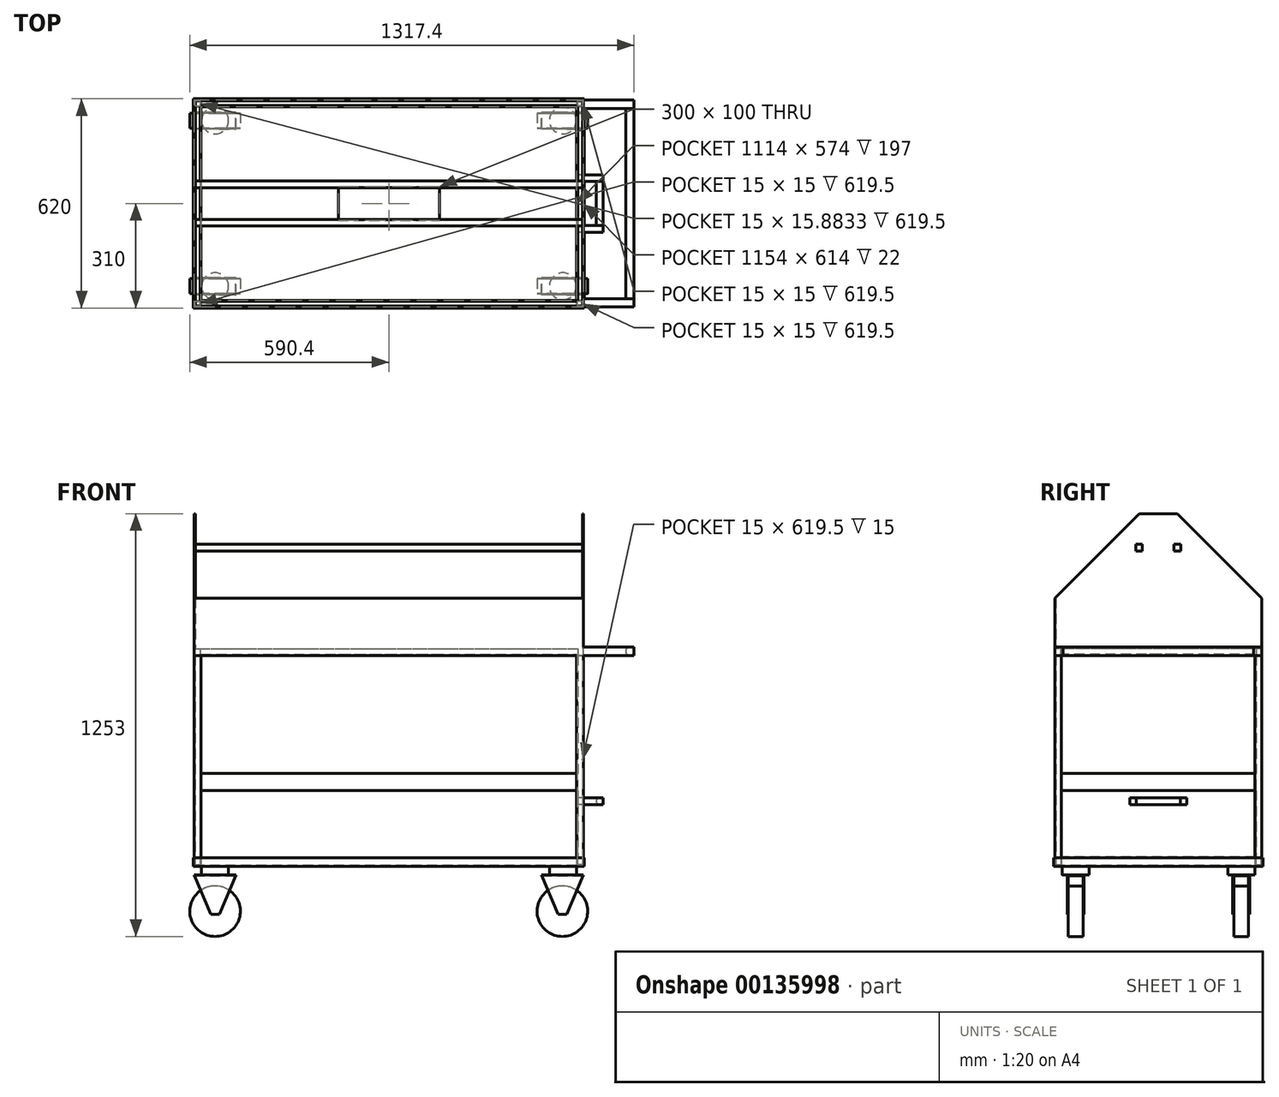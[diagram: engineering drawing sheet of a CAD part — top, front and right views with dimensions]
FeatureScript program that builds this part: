
annotation { "Feature Type Name" : "Feature", "Feature Type Description" : "" }
export const myFeature = defineFeature(function(context is Context, id is Id, definition is map)
    precondition{}
    {
        {
            var Q0;
            Q0=qCreatedBy(makeId("Top.planeOp"),FACE);
            var sketch = newSketch(context, id + "F0", { "sketchPlane" : qUnion([Q0])});
            skLineSegment(sketch, "E0.bottom", {"start": v(-580, 310) * mm, "end": v(580, 310) * mm});
            skLineSegment(sketch, "E0.top", {"start": v(-580, -310) * mm, "end": v(580, -310) * mm});
            skLineSegment(sketch, "E0.left", {"start": v(-580, 310) * mm, "end": v(-580, -310) * mm});
            skLineSegment(sketch, "E0.right", {"start": v(580, 310) * mm, "end": v(580, -310) * mm});
            skPoint(sketch, "E0.middle", {"position": v(0, 0) * mm});
            skLineSegment(sketch, "E1.bottom", {"start": v(-560, 290) * mm, "end": v(560, 290) * mm});
            skLineSegment(sketch, "E1.top", {"start": v(-560, -290) * mm, "end": v(560, -290) * mm});
            skLineSegment(sketch, "E1.left", {"start": v(-560, 290) * mm, "end": v(-560, -290) * mm});
            skLineSegment(sketch, "E1.right", {"start": v(560, 290) * mm, "end": v(560, -290) * mm});
            skSolve(sketch);
        }
        {
            var Q0;
            Q0=makeQuery(id+"F0.imprint","IMPRINT",FACE,{"disambiguationData":[TD([[makeQuery(id+"F0.imprint","IMPRINT",EDGE,{"derivedFrom":sQuery(id+"F0.wireOp",EDGE,"E1.bottom")}),-1.0]])]});
            extrude(context, id + "F1", {"entities" : qUnion([Q0]), "depth" : 350 * mm});
        }
        {
            var Q0;
            Q0=makeQuery(id+"F0.imprint","IMPRINT",FACE,{"disambiguationData":[TD([[makeQuery(id+"F0.imprint","IMPRINT",EDGE,{"derivedFrom":sQuery(id+"F0.wireOp",EDGE,"E1.bottom")}),-1.0]])]});
            extrude(context, id + "F2", {"entities" : qUnion([Q0]), "operationType" : NewBodyOperationType.ADD, "oppositeDirection" : true, "depth" : 250 * mm});
        }
        {
            var Q0;
            Q0=makeQuery(id+"F0.imprint","IMPRINT",FACE,{"disambiguationData":[TD([[makeQuery(id+"F0.imprint","IMPRINT",EDGE,{"derivedFrom":sQuery(id+"F0.wireOp",EDGE,"E1.bottom")}),-1.0]])]});
            extrude(context, id + "F3", {"entities" : qUnion([Q0]), "operationType" : NewBodyOperationType.REMOVE, "oppositeDirection" : true, "depth" : 50 * mm});
        }
        {
            var Q0;
            Q0=makeQuery(id+"F3.boolean.opBoolean","COPY",FACE,{"derivedFrom":makeQuery(id+"F3.opExtrude","CAP_FACE",FACE,{"disambiguationData":[OSD([sQuery(id+"F0.wireOp",EDGE,"E1.bottom"),sQuery(id+"F0.wireOp",EDGE,"E1.top"),sQuery(id+"F0.wireOp",EDGE,"E1.left"),sQuery(id+"F0.wireOp",EDGE,"E1.right")])],"isStart":false})});
            shell(context, id + "F4", {"entities" : qUnion([Q0]), "thickness" : 3 * mm});
        }
        {
            var Q0;
            Q0=makeQuery(id+"F2.opExtrude","CAP_FACE",FACE,{"disambiguationData":[OSD([sQuery(id+"F0.wireOp",EDGE,"E1.bottom"),sQuery(id+"F0.wireOp",EDGE,"E1.top"),sQuery(id+"F0.wireOp",EDGE,"E1.left"),sQuery(id+"F0.wireOp",EDGE,"E1.right")])],"isStart":false});
            var sketch = newSketch(context, id + "F5", { "sketchPlane" : qUnion([Q0])});
            skLineSegment(sketch, "E2.bottom", {"start": v(-580, 310) * mm, "end": v(580, 310) * mm});
            skLineSegment(sketch, "E2.top", {"start": v(-580, -310) * mm, "end": v(580, -310) * mm});
            skLineSegment(sketch, "E2.left", {"start": v(-580, 310) * mm, "end": v(-580, -310) * mm});
            skLineSegment(sketch, "E2.right", {"start": v(580, 310) * mm, "end": v(580, -310) * mm});
            skPoint(sketch, "E2.middle", {"position": v(0, 0) * mm});
            skSolve(sketch);
        }
        {
            var Q0;
            Q0=makeQuery(id+"F5.imprint","IMPRINT",FACE,{"disambiguationData":[TD([[makeQuery(id+"F5.imprint","IMPRINT",EDGE,{"derivedFrom":sQuery(id+"F5.wireOp",EDGE,"E2.bottom")}),-1.0]])]});
            var Q1;
            Q1=makeQuery(id+"F5.imprint","IMPRINT",FACE,{"disambiguationData":[TD([[makeQuery(id+"F5.imprint","IMPRINT",EDGE,{"derivedFrom":makeQuery(id+"F2.opExtrude","CAP_EDGE",EDGE,{"disambiguationData":[OSD([sQuery(id+"F0.wireOp",EDGE,"E1.bottom")])],"isStart":false})}),1.0]])]});
            extrude(context, id + "F6", {"entities" : qUnion([Q0, Q1]), "depth" : 25 * mm});
        }
        {
            var Q0;
            Q0=makeQuery(id+"F6.opExtrude","CAP_FACE",FACE,{"disambiguationData":[OSD([sQuery(id+"F5.wireOp",EDGE,"E2.bottom"),sQuery(id+"F5.wireOp",EDGE,"E2.top"),sQuery(id+"F5.wireOp",EDGE,"E2.left"),sQuery(id+"F5.wireOp",EDGE,"E2.right")])],"isStart":true});
            var Q1;
            Q1=makeQuery(id+"F6.opExtrude","SWEPT_BODY",BODY,{"disambiguationData":[OSD([sQuery(id+"F5.wireOp",EDGE,"E2.bottom"),sQuery(id+"F5.wireOp",EDGE,"E2.top"),sQuery(id+"F5.wireOp",EDGE,"E2.left"),sQuery(id+"F5.wireOp",EDGE,"E2.right")])]});
            shell(context, id + "F7", {"entities" : qUnion([Q0]), "parts" : qUnion([Q1]), "thickness" : 3 * mm});
        }
        {
            var Q0;
            Q0=makeQuery(id+"F7.opShell","OFFSET_FACE",FACE,{"disambiguationData":[OSD([sQuery(id+"F5.wireOp",EDGE,"E2.bottom"),sQuery(id+"F5.wireOp",EDGE,"E2.top"),sQuery(id+"F5.wireOp",EDGE,"E2.left"),sQuery(id+"F5.wireOp",EDGE,"E2.right")])]});
            var sketch = newSketch(context, id + "F8", { "sketchPlane" : qUnion([Q0])});
            skLineSegment(sketch, "E3.bottom", {"start": v(-577, 307) * mm, "end": v(-557, 307) * mm});
            skLineSegment(sketch, "E3.top", {"start": v(-577, 286.12) * mm, "end": v(-557, 286.12) * mm});
            skLineSegment(sketch, "E3.left", {"start": v(-577, 307) * mm, "end": v(-577, 286.12) * mm});
            skLineSegment(sketch, "E3.right", {"start": v(-557, 307) * mm, "end": v(-557, 286.12) * mm});
            skLineSegment(sketch, "E4.bottom", {"start": v(577, 307) * mm, "end": v(557, 307) * mm});
            skLineSegment(sketch, "E4.top", {"start": v(577, 287) * mm, "end": v(557, 287) * mm});
            skLineSegment(sketch, "E4.left", {"start": v(577, 307) * mm, "end": v(577, 287) * mm});
            skLineSegment(sketch, "E4.right", {"start": v(557, 307) * mm, "end": v(557, 287) * mm});
            skLineSegment(sketch, "E5.bottom", {"start": v(577, -307) * mm, "end": v(557, -307) * mm});
            skLineSegment(sketch, "E5.top", {"start": v(577, -287) * mm, "end": v(557, -287) * mm});
            skLineSegment(sketch, "E5.left", {"start": v(577, -307) * mm, "end": v(577, -287) * mm});
            skLineSegment(sketch, "E5.right", {"start": v(557, -307) * mm, "end": v(557, -287) * mm});
            skLineSegment(sketch, "E6.bottom", {"start": v(-577, -307) * mm, "end": v(-557, -307) * mm});
            skLineSegment(sketch, "E6.top", {"start": v(-577, -287) * mm, "end": v(-557, -287) * mm});
            skLineSegment(sketch, "E6.left", {"start": v(-577, -307) * mm, "end": v(-577, -287) * mm});
            skLineSegment(sketch, "E6.right", {"start": v(-557, -307) * mm, "end": v(-557, -287) * mm});
            skSolve(sketch);
        }
        {
            var Q0;
            Q0=makeQuery(id+"F8.imprint","IMPRINT",FACE,{"disambiguationData":[TD([[makeQuery(id+"F8.imprint","IMPRINT",EDGE,{"derivedFrom":sQuery(id+"F8.wireOp",EDGE,"E3.bottom")}),-1.0]])]});
            var Q1;
            Q1=makeQuery(id+"F8.imprint","IMPRINT",FACE,{"disambiguationData":[TD([[makeQuery(id+"F8.imprint","IMPRINT",EDGE,{"derivedFrom":sQuery(id+"F8.wireOp",EDGE,"E6.bottom")}),1.0]])]});
            var Q2;
            Q2=makeQuery(id+"F8.imprint","IMPRINT",FACE,{"disambiguationData":[TD([[makeQuery(id+"F8.imprint","IMPRINT",EDGE,{"derivedFrom":sQuery(id+"F8.wireOp",EDGE,"E4.bottom")}),-1.0]])]});
            var Q3;
            Q3=makeQuery(id+"F8.imprint","IMPRINT",FACE,{"disambiguationData":[TD([[makeQuery(id+"F8.imprint","IMPRINT",EDGE,{"derivedFrom":sQuery(id+"F8.wireOp",EDGE,"E5.bottom")}),1.0]])]});
            extrude(context, id + "F9", {"entities" : qUnion([Q0, Q1, Q2, Q3]), "depth" : 622 * mm});
        }
        {
            var Q0;
            Q0=makeQuery(id+"F9.opExtrude","CAP_FACE",FACE,{"disambiguationData":[OSD([sQuery(id+"F8.wireOp",EDGE,"E3.bottom"),sQuery(id+"F8.wireOp",EDGE,"E3.top"),sQuery(id+"F8.wireOp",EDGE,"E3.left"),sQuery(id+"F8.wireOp",EDGE,"E3.right")])],"isStart":false});
            var Q1;
            Q1=makeQuery(id+"F9.opExtrude","CAP_FACE",FACE,{"disambiguationData":[OSD([sQuery(id+"F8.wireOp",EDGE,"E4.bottom"),sQuery(id+"F8.wireOp",EDGE,"E4.top"),sQuery(id+"F8.wireOp",EDGE,"E4.left"),sQuery(id+"F8.wireOp",EDGE,"E4.right")])],"isStart":false});
            var Q2;
            Q2=makeQuery(id+"F9.opExtrude","CAP_FACE",FACE,{"disambiguationData":[OSD([sQuery(id+"F8.wireOp",EDGE,"E5.bottom"),sQuery(id+"F8.wireOp",EDGE,"E5.top"),sQuery(id+"F8.wireOp",EDGE,"E5.left"),sQuery(id+"F8.wireOp",EDGE,"E5.right")])],"isStart":false});
            var Q3;
            Q3=makeQuery(id+"F9.opExtrude","CAP_FACE",FACE,{"disambiguationData":[OSD([sQuery(id+"F8.wireOp",EDGE,"E6.bottom"),sQuery(id+"F8.wireOp",EDGE,"E6.top"),sQuery(id+"F8.wireOp",EDGE,"E6.left"),sQuery(id+"F8.wireOp",EDGE,"E6.right")])],"isStart":false});
            shell(context, id + "F10", {"entities" : qUnion([Q0, Q1, Q2, Q3]), "thickness" : 2.5 * mm});
        }
        {
            var Q0;
            Q0=makeQuery(id+"F1.opExtrude","CAP_FACE",FACE,{"disambiguationData":[OSD([sQuery(id+"F0.wireOp",EDGE,"E1.bottom"),sQuery(id+"F0.wireOp",EDGE,"E1.top"),sQuery(id+"F0.wireOp",EDGE,"E1.left"),sQuery(id+"F0.wireOp",EDGE,"E1.right")])],"isStart":false});
            var sketch = newSketch(context, id + "F11", { "sketchPlane" : qUnion([Q0])});
            skLineSegment(sketch, "E7.bottom", {"start": v(-577, 307) * mm, "end": v(577, 307) * mm});
            skLineSegment(sketch, "E7.top", {"start": v(-577, -307) * mm, "end": v(577, -307) * mm});
            skLineSegment(sketch, "E7.left", {"start": v(-577, 307) * mm, "end": v(-577, -307) * mm});
            skLineSegment(sketch, "E7.right", {"start": v(577, 307) * mm, "end": v(577, -307) * mm});
            skPoint(sketch, "E7.middle", {"position": v(0, 0) * mm});
            skSolve(sketch);
        }
        {
            var Q0;
            Q0=makeQuery(id+"F11.imprint","IMPRINT",FACE,{"disambiguationData":[TD([[makeQuery(id+"F11.imprint","IMPRINT",EDGE,{"derivedFrom":sQuery(id+"F11.wireOp",EDGE,"E7.bottom")}),-1.0]])]});
            extrude(context, id + "F12", {"entities" : qUnion([Q0]), "depth" : 20 * mm});
        }
        {
            var Q0;
            Q0=makeQuery(id+"F12.opExtrude","CAP_FACE",FACE,{"disambiguationData":[OSD([sQuery(id+"F0.wireOp",EDGE,"E1.bottom"),sQuery(id+"F0.wireOp",EDGE,"E1.top"),sQuery(id+"F0.wireOp",EDGE,"E1.left"),sQuery(id+"F0.wireOp",EDGE,"E1.right"),sQuery(id+"F33Y3pSXNLTwZaf_1.wireOp",EDGE,"aj6i3p2y-FQMm-kt0m-HM5S-YSBZW6WqoPSV"),sQuery(id+"F33Y3pSXNLTwZaf_1.wireOp",EDGE,"CZkD7vCU-3LIm-oKTz-ViHN-LZSoxyDXXNPL"),sQuery(id+"F33Y3pSXNLTwZaf_1.wireOp",EDGE,"GoPMTof5-LQTN-zhxn-LOWR-9AagRQIQ8QUd"),sQuery(id+"F33Y3pSXNLTwZaf_1.wireOp",EDGE,"wMd1c553-RlNz-IpVQ-kuJJ-040cahTZoC20"),sQuery(id+"F1xDDwHVUP71mYk_1.wireOp",EDGE,"cAczI6bI-1LX6-aqdC-7smG-W6fWwqjZtxQi"),sQuery(id+"F1xDDwHVUP71mYk_1.wireOp",EDGE,"ZDiwBjCm-7RDb-v4AQ-MkSP-Jul3cs5UostI"),sQuery(id+"F1xDDwHVUP71mYk_1.wireOp",EDGE,"UBjxF51A-ai0a-dGns-wWAK-TeR3P6ofujuV"),sQuery(id+"F1xDDwHVUP71mYk_1.wireOp",EDGE,"N02EDcg1-XUBP-QACv-A8dY-pTifU5Cc8YaH"),sQuery(id+"F11.wireOp",EDGE,"E7.bottom"),sQuery(id+"F11.wireOp",EDGE,"E7.top"),sQuery(id+"F11.wireOp",EDGE,"E7.left"),sQuery(id+"F11.wireOp",EDGE,"E7.right")])],"isStart":false});
            var sketch = newSketch(context, id + "F13", { "sketchPlane" : qUnion([Q0])});
            skLineSegment(sketch, "E8.bottom", {"start": v(-577, 307) * mm, "end": v(-574, 307) * mm});
            skLineSegment(sketch, "E8.top", {"start": v(-577, -307) * mm, "end": v(-574, -307) * mm});
            skLineSegment(sketch, "E8.left", {"start": v(-577, 307) * mm, "end": v(-577, -307) * mm});
            skLineSegment(sketch, "E8.right", {"start": v(-574, 307) * mm, "end": v(-574, -307) * mm});
            skLineSegment(sketch, "E9.bottom", {"start": v(577, -307) * mm, "end": v(574, -307) * mm});
            skLineSegment(sketch, "E9.top", {"start": v(577, 307) * mm, "end": v(574, 307) * mm});
            skLineSegment(sketch, "E9.left", {"start": v(577, -307) * mm, "end": v(577, 307) * mm});
            skLineSegment(sketch, "E9.right", {"start": v(574, -307) * mm, "end": v(574, 307) * mm});
            skSolve(sketch);
        }
        {
            var Q0;
            Q0=makeQuery(id+"F13.imprint","IMPRINT",FACE,{"disambiguationData":[TD([[makeQuery(id+"F13.imprint","IMPRINT",EDGE,{"derivedFrom":sQuery(id+"F13.wireOp",EDGE,"E9.bottom")}),1.0]])]});
            var Q1;
            Q1=makeQuery(id+"F13.imprint","IMPRINT",FACE,{"disambiguationData":[TD([[makeQuery(id+"F13.imprint","IMPRINT",EDGE,{"derivedFrom":sQuery(id+"F13.wireOp",EDGE,"E8.bottom")}),-1.0]])]});
            extrude(context, id + "F14", {"entities" : qUnion([Q0, Q1]), "operationType" : NewBodyOperationType.ADD, "depth" : 400 * mm});
        }
        {
            var Q0;
            Q0=makeQuery(id+"F14.boolean.opBoolean","MERGE",FACE,{"derivedFrom":[makeQuery(id+"F12.opExtrude","SWEPT_FACE",FACE,{"disambiguationData":[OSD([sQuery(id+"F11.wireOp",EDGE,"E7.right")])]}),makeQuery(id+"F14.opExtrude","SWEPT_FACE",FACE,{"disambiguationData":[OSD([sQuery(id+"F13.wireOp",EDGE,"E9.left")])]})]});
            var sketch = newSketch(context, id + "F15", { "sketchPlane" : qUnion([Q0])});
            skLineSegment(sketch, "E10", {"start": v(-307, 770) * mm, "end": v(-57, 770) * mm});
            skLineSegment(sketch, "E11", {"start": v(-307, 770) * mm, "end": v(-307, 520) * mm});
            skLineSegment(sketch, "E12", {"start": v(-307, 520) * mm, "end": v(-57, 770) * mm});
            skLineSegment(sketch, "E13", {"start": v(307, 770) * mm, "end": v(57, 770) * mm});
            skLineSegment(sketch, "E14", {"start": v(57, 770) * mm, "end": v(307, 520) * mm});
            skLineSegment(sketch, "E15", {"start": v(307, 520) * mm, "end": v(307, 770) * mm});
            skLineSegment(sketch, "E16", {"start": v(-307, 770) * mm, "end": v(-307, 670) * mm, "construction": true});
            skLineSegment(sketch, "E17.bottom", {"start": v(-77.82, 670.93) * mm, "end": v(-57.82, 670.93) * mm});
            skLineSegment(sketch, "E17.top", {"start": v(-77.82, 650.93) * mm, "end": v(-57.82, 650.93) * mm});
            skLineSegment(sketch, "E17.left", {"start": v(-77.82, 670.93) * mm, "end": v(-77.82, 650.93) * mm});
            skLineSegment(sketch, "E17.right", {"start": v(-57.82, 670.93) * mm, "end": v(-57.82, 650.93) * mm});
            skPoint(sketch, "E17.middle", {"position": v(-67.82, 660.93) * mm});
            skLineSegment(sketch, "E18.bottom", {"start": v(31.3, 667.95) * mm, "end": v(51.3, 667.95) * mm});
            skLineSegment(sketch, "E18.top", {"start": v(31.3, 647.95) * mm, "end": v(51.3, 647.95) * mm});
            skLineSegment(sketch, "E18.left", {"start": v(31.3, 667.95) * mm, "end": v(31.3, 647.95) * mm});
            skLineSegment(sketch, "E18.right", {"start": v(51.3, 667.95) * mm, "end": v(51.3, 647.95) * mm});
            skPoint(sketch, "E18.middle", {"position": v(41.3, 657.95) * mm});
            skSolve(sketch);
        }
        {
            var Q0;
            Q0=makeQuery(id+"F15.imprint","IMPRINT",FACE,{"disambiguationData":[TD([[makeQuery(id+"F15.imprint","IMPRINT",EDGE,{"derivedFrom":sQuery(id+"F15.wireOp",EDGE,"E10")}),1.0]])]});
            var Q1;
            Q1=makeQuery(id+"F15.imprint","IMPRINT",FACE,{"disambiguationData":[TD([[makeQuery(id+"F15.imprint","IMPRINT",EDGE,{"derivedFrom":sQuery(id+"F15.wireOp",EDGE,"E13")}),1.0]])]});
            extrude(context, id + "F16", {"entities" : qUnion([Q0, Q1]), "operationType" : NewBodyOperationType.REMOVE, "oppositeDirection" : true, "depth" : 1160 * mm});
        }
        {
            var Q0;
            Q0=makeQuery(id+"F14.boolean.opBoolean","MERGE",FACE,{"derivedFrom":[makeQuery(id+"F12.opExtrude","SWEPT_FACE",FACE,{"disambiguationData":[OSD([sQuery(id+"F11.wireOp",EDGE,"E7.right")])]}),makeQuery(id+"F14.opExtrude","SWEPT_FACE",FACE,{"disambiguationData":[OSD([sQuery(id+"F13.wireOp",EDGE,"E9.left")])]})]});
            var sketch = newSketch(context, id + "F17", { "sketchPlane" : qUnion([Q0])});
            skLineSegment(sketch, "E19", {"start": v(-57, 770) * mm, "end": v(-57, 670) * mm, "construction": true});
            skLineSegment(sketch, "E20", {"start": v(57, 770) * mm, "end": v(57, 670) * mm, "construction": true});
            skLineSegment(sketch, "E21.bottom", {"start": v(-67, 680) * mm, "end": v(-47, 680) * mm});
            skLineSegment(sketch, "E21.top", {"start": v(-67, 660) * mm, "end": v(-47, 660) * mm});
            skLineSegment(sketch, "E21.left", {"start": v(-67, 680) * mm, "end": v(-67, 660) * mm});
            skLineSegment(sketch, "E21.right", {"start": v(-47, 680) * mm, "end": v(-47, 660) * mm});
            skPoint(sketch, "E21.middle", {"position": v(-57, 670) * mm});
            skLineSegment(sketch, "E22.bottom", {"start": v(47, 680) * mm, "end": v(67, 680) * mm});
            skLineSegment(sketch, "E22.top", {"start": v(47, 660) * mm, "end": v(67, 660) * mm});
            skLineSegment(sketch, "E22.left", {"start": v(47, 680) * mm, "end": v(47, 660) * mm});
            skLineSegment(sketch, "E22.right", {"start": v(67, 680) * mm, "end": v(67, 660) * mm});
            skPoint(sketch, "E22.middle", {"position": v(57, 670) * mm});
            skSolve(sketch);
        }
        {
            var Q0;
            Q0=makeQuery(id+"F17.imprint","IMPRINT",FACE,{"disambiguationData":[TD([[makeQuery(id+"F17.imprint","IMPRINT",EDGE,{"derivedFrom":sQuery(id+"F17.wireOp",EDGE,"E21.bottom")}),-1.0]])]});
            var Q1;
            Q1=makeQuery(id+"F17.imprint","IMPRINT",FACE,{"disambiguationData":[TD([[makeQuery(id+"F17.imprint","IMPRINT",EDGE,{"derivedFrom":sQuery(id+"F17.wireOp",EDGE,"E22.bottom")}),-1.0]])]});
            extrude(context, id + "F18", {"entities" : qUnion([Q0, Q1]), "oppositeDirection" : true, "offsetDistance" : 25 * mm, "depth" : 1153 * mm});
        }
        {
            var Q0;
            Q0=makeQuery(id+"F12.opExtrude","CAP_FACE",FACE,{"disambiguationData":[OSD([sQuery(id+"F0.wireOp",EDGE,"E1.bottom"),sQuery(id+"F0.wireOp",EDGE,"E1.top"),sQuery(id+"F0.wireOp",EDGE,"E1.left"),sQuery(id+"F0.wireOp",EDGE,"E1.right"),sQuery(id+"F33Y3pSXNLTwZaf_1.wireOp",EDGE,"aj6i3p2y-FQMm-kt0m-HM5S-YSBZW6WqoPSV"),sQuery(id+"F33Y3pSXNLTwZaf_1.wireOp",EDGE,"CZkD7vCU-3LIm-oKTz-ViHN-LZSoxyDXXNPL"),sQuery(id+"F33Y3pSXNLTwZaf_1.wireOp",EDGE,"GoPMTof5-LQTN-zhxn-LOWR-9AagRQIQ8QUd"),sQuery(id+"F33Y3pSXNLTwZaf_1.wireOp",EDGE,"wMd1c553-RlNz-IpVQ-kuJJ-040cahTZoC20"),sQuery(id+"F1xDDwHVUP71mYk_1.wireOp",EDGE,"cAczI6bI-1LX6-aqdC-7smG-W6fWwqjZtxQi"),sQuery(id+"F1xDDwHVUP71mYk_1.wireOp",EDGE,"ZDiwBjCm-7RDb-v4AQ-MkSP-Jul3cs5UostI"),sQuery(id+"F1xDDwHVUP71mYk_1.wireOp",EDGE,"UBjxF51A-ai0a-dGns-wWAK-TeR3P6ofujuV"),sQuery(id+"F1xDDwHVUP71mYk_1.wireOp",EDGE,"N02EDcg1-XUBP-QACv-A8dY-pTifU5Cc8YaH"),sQuery(id+"F11.wireOp",EDGE,"E7.bottom"),sQuery(id+"F11.wireOp",EDGE,"E7.top"),sQuery(id+"F11.wireOp",EDGE,"E7.left"),sQuery(id+"F11.wireOp",EDGE,"E7.right")])],"isStart":false});
            var sketch = newSketch(context, id + "F19", { "sketchPlane" : qUnion([Q0])});
            skLineSegment(sketch, "E23.bottom", {"start": v(-574, 307) * mm, "end": v(574, 307) * mm});
            skLineSegment(sketch, "E23.top", {"start": v(-574, 304) * mm, "end": v(574, 304) * mm});
            skLineSegment(sketch, "E23.left", {"start": v(-574, 307) * mm, "end": v(-574, 304) * mm});
            skLineSegment(sketch, "E23.right", {"start": v(574, 307) * mm, "end": v(574, 304) * mm});
            skLineSegment(sketch, "E24.bottom", {"start": v(-574, -307) * mm, "end": v(574, -307) * mm});
            skLineSegment(sketch, "E24.top", {"start": v(-574, -304) * mm, "end": v(574, -304) * mm});
            skLineSegment(sketch, "E24.left", {"start": v(-574, -307) * mm, "end": v(-574, -304) * mm});
            skLineSegment(sketch, "E24.right", {"start": v(574, -307) * mm, "end": v(574, -304) * mm});
            skSolve(sketch);
        }
        {
            var Q0;
            Q0=makeQuery(id+"F19.imprint","IMPRINT",FACE,{"disambiguationData":[TD([[makeQuery(id+"F19.imprint","IMPRINT",EDGE,{"derivedFrom":sQuery(id+"F19.wireOp",EDGE,"E24.bottom")}),1.0]])]});
            var Q1;
            Q1=makeQuery(id+"F19.imprint","IMPRINT",FACE,{"disambiguationData":[TD([[makeQuery(id+"F19.imprint","IMPRINT",EDGE,{"derivedFrom":sQuery(id+"F19.wireOp",EDGE,"E23.bottom")}),-1.0]])]});
            extrude(context, id + "F20", {"entities" : qUnion([Q0, Q1]), "operationType" : NewBodyOperationType.ADD, "depth" : 20 * mm});
        }
        {
            var Q0;
            Q0=makeQuery(id+"F2.opExtrude","SWEPT_FACE",FACE,{"disambiguationData":[OSD([sQuery(id+"F0.wireOp",EDGE,"E1.right")])]});
            var sketch = newSketch(context, id + "F21", { "sketchPlane" : qUnion([Q0])});
            skLineSegment(sketch, "E25", {"start": v(0, -82.19) * mm, "end": v(-75, -82.19) * mm, "construction": true});
            skLineSegment(sketch, "E26", {"start": v(0, -82.19) * mm, "end": v(75, -82.19) * mm, "construction": true});
            skLineSegment(sketch, "E27.bottom", {"start": v(-85, -72.19) * mm, "end": v(-65, -72.19) * mm});
            skLineSegment(sketch, "E27.top", {"start": v(-85, -92.19) * mm, "end": v(-65, -92.19) * mm});
            skLineSegment(sketch, "E27.left", {"start": v(-85, -72.19) * mm, "end": v(-85, -92.19) * mm});
            skLineSegment(sketch, "E27.right", {"start": v(-65, -72.19) * mm, "end": v(-65, -92.19) * mm});
            skPoint(sketch, "E27.middle", {"position": v(-75, -82.19) * mm});
            skLineSegment(sketch, "E28.bottom", {"start": v(65, -72.19) * mm, "end": v(85, -72.19) * mm});
            skLineSegment(sketch, "E28.top", {"start": v(65, -92.19) * mm, "end": v(85, -92.19) * mm});
            skLineSegment(sketch, "E28.left", {"start": v(65, -72.19) * mm, "end": v(65, -92.19) * mm});
            skLineSegment(sketch, "E28.right", {"start": v(85, -72.19) * mm, "end": v(85, -92.19) * mm});
            skPoint(sketch, "E28.middle", {"position": v(75, -82.19) * mm});
            skSolve(sketch);
        }
        {
            var Q0;
            Q0=makeQuery(id+"F21.imprint","IMPRINT",FACE,{"disambiguationData":[TD([[makeQuery(id+"F21.imprint","IMPRINT",EDGE,{"derivedFrom":sQuery(id+"F21.wireOp",EDGE,"E27.bottom")}),-1.0]])]});
            var Q1;
            Q1=makeQuery(id+"F21.imprint","IMPRINT",FACE,{"disambiguationData":[TD([[makeQuery(id+"F21.imprint","IMPRINT",EDGE,{"derivedFrom":sQuery(id+"F21.wireOp",EDGE,"E28.bottom")}),-1.0]])]});
            extrude(context, id + "F22", {"entities" : qUnion([Q0, Q1]), "operationType" : NewBodyOperationType.ADD, "depth" : 75 * mm});
        }
        {
            var Q0;
            Q0=makeQuery(id+"F22.opExtrude","SWEPT_FACE",FACE,{"disambiguationData":[OSD([sQuery(id+"F21.wireOp",EDGE,"E28.left")])]});
            var sketch = newSketch(context, id + "F23", { "sketchPlane" : qUnion([Q0])});
            skCircle(sketch, "E29", {"center": v(625, -82.19) * mm, "radius": 10 * mm});
            skSolve(sketch);
        }
        {
            var Q0;
            {var subQ0=sQuery(id+"F23.wireOp",EDGE,"E29");var subQ1=sQuery(id+"F21.wireOp",EDGE,"E28.left");var subQ3=makeQuery(id+"F23.imprint","INTERSECT",VERTEX,{"derivedFrom":[makeQuery(id+"F22.opExtrude","CAP_EDGE",EDGE,{"disambiguationData":[OSD([subQ1])],"isStart":false}),subQ0]});Q0=makeQuery(id+"F23.imprint","IMPRINT",FACE,{"disambiguationData":[TD([[makeQuery(id+"F23.imprint","IMPRINT",EDGE,{"disambiguationData":[TD([[subQ3,-1.0]])],"derivedFrom":subQ0}),1.0]])]});}
            extrude(context, id + "F24", {"entities" : qUnion([Q0]), "operationType" : NewBodyOperationType.ADD, "depth" : 140 * mm});
        }
        {
            var Q0;
            Q0=makeQuery(id+"F14.boolean.opBoolean","MERGE",FACE,{"derivedFrom":[makeQuery(id+"F12.opExtrude","SWEPT_FACE",FACE,{"disambiguationData":[OSD([sQuery(id+"F11.wireOp",EDGE,"E7.right")])]}),makeQuery(id+"F14.opExtrude","SWEPT_FACE",FACE,{"disambiguationData":[OSD([sQuery(id+"F13.wireOp",EDGE,"E9.left")])]})]});
            var sketch = newSketch(context, id + "F25", { "sketchPlane" : qUnion([Q0])});
            skLineSegment(sketch, "E30.bottom", {"start": v(-307, 350) * mm, "end": v(-282, 350) * mm});
            skLineSegment(sketch, "E30.top", {"start": v(-307, 375) * mm, "end": v(-282, 375) * mm});
            skLineSegment(sketch, "E30.left", {"start": v(-307, 350) * mm, "end": v(-307, 375) * mm});
            skLineSegment(sketch, "E30.right", {"start": v(-282, 350) * mm, "end": v(-282, 375) * mm});
            skLineSegment(sketch, "E31.bottom", {"start": v(307, 350) * mm, "end": v(282, 350) * mm});
            skLineSegment(sketch, "E31.top", {"start": v(307, 375) * mm, "end": v(282, 375) * mm});
            skLineSegment(sketch, "E31.left", {"start": v(307, 350) * mm, "end": v(307, 375) * mm});
            skLineSegment(sketch, "E31.right", {"start": v(282, 350) * mm, "end": v(282, 375) * mm});
            skSolve(sketch);
        }
        {
            var Q0;
            Q0=makeQuery(id+"F25.imprint","IMPRINT",FACE,{"disambiguationData":[TD([[makeQuery(id+"F25.imprint","IMPRINT",EDGE,{"derivedFrom":sQuery(id+"F25.wireOp",EDGE,"E30.bottom")}),-1.0]])]});
            var Q1;
            Q1=makeQuery(id+"F25.imprint","IMPRINT",FACE,{"disambiguationData":[TD([[makeQuery(id+"F25.imprint","IMPRINT",EDGE,{"derivedFrom":sQuery(id+"F25.wireOp",EDGE,"E31.bottom")}),-1.0]])]});
            extrude(context, id + "F26", {"entities" : qUnion([Q0, Q1]), "operationType" : NewBodyOperationType.ADD, "depth" : 150 * mm});
        }
        {
            var Q0;
            Q0=makeQuery(id+"F26.opExtrude","SWEPT_FACE",FACE,{"disambiguationData":[OSD([sQuery(id+"F25.wireOp",EDGE,"E31.right")])]});
            var sketch = newSketch(context, id + "F27", { "sketchPlane" : qUnion([Q0])});
            skPoint(sketch, "E32.endSnap0", {"position": v(652, 350) * mm});
            skCircle(sketch, "E33", {"center": v(714.5, 362.5) * mm, "radius": 12.5 * mm});
            skSolve(sketch);
        }
        {
            var Q0;
            {var subQ0=sQuery(id+"F27.wireOp",EDGE,"E33");var subQ1=sQuery(id+"F25.wireOp",EDGE,"E31.right");var subQ3=makeQuery(id+"F27.imprint","INTERSECT",VERTEX,{"derivedFrom":[makeQuery(id+"F26.opExtrude","CAP_EDGE",EDGE,{"disambiguationData":[OSD([subQ1])],"isStart":false}),subQ0]});Q0=makeQuery(id+"F27.imprint","IMPRINT",FACE,{"disambiguationData":[TD([[makeQuery(id+"F27.imprint","IMPRINT",EDGE,{"disambiguationData":[TD([[subQ3,-1.0]])],"derivedFrom":subQ0}),1.0]])]});}
            extrude(context, id + "F28", {"entities" : qUnion([Q0]), "operationType" : NewBodyOperationType.ADD, "depth" : 580 * mm});
        }
        {
            var Q0;
            Q0=makeQuery(id+"F6.opExtrude","CAP_FACE",FACE,{"disambiguationData":[OSD([sQuery(id+"F5.wireOp",EDGE,"E2.bottom"),sQuery(id+"F5.wireOp",EDGE,"E2.top"),sQuery(id+"F5.wireOp",EDGE,"E2.left"),sQuery(id+"F5.wireOp",EDGE,"E2.right")])],"isStart":false});
            var sketch = newSketch(context, id + "F29", { "sketchPlane" : qUnion([Q0])});
            skLineSegment(sketch, "E34", {"start": v(-580, 310) * mm, "end": v(-580, -310) * mm});
            skLineSegment(sketch, "E35", {"start": v(-580, -310) * mm, "end": v(-580, -310) * mm});
            skLineSegment(sketch, "E36", {"start": v(580, -310) * mm, "end": v(580, -310) * mm});
            skLineSegment(sketch, "E37", {"start": v(580, 310) * mm, "end": v(580, 310) * mm});
            skCircle(sketch, "E38", {"center": v(-515.4, 245.4) * mm, "radius": 40 * mm});
            skCircle(sketch, "E39", {"center": v(516.1, 245.4) * mm, "radius": 40 * mm});
            skCircle(sketch, "E40", {"center": v(516.1, -246.1) * mm, "radius": 40 * mm});
            skCircle(sketch, "E41", {"center": v(-515.4, -246.1) * mm, "radius": 40 * mm});
            skSolve(sketch);
        }
        {
            var Q0;
            Q0=makeQuery(id+"F29.imprint","IMPRINT",FACE,{"disambiguationData":[TD([[makeQuery(id+"F29.imprint","IMPRINT",EDGE,{"derivedFrom":sQuery(id+"F29.wireOp",EDGE,"E38")}),1.0]])]});
            var Q1;
            Q1=makeQuery(id+"F29.imprint","IMPRINT",FACE,{"disambiguationData":[TD([[makeQuery(id+"F29.imprint","IMPRINT",EDGE,{"derivedFrom":sQuery(id+"F29.wireOp",EDGE,"E39")}),1.0]])]});
            var Q2;
            Q2=makeQuery(id+"F29.imprint","IMPRINT",FACE,{"disambiguationData":[TD([[makeQuery(id+"F29.imprint","IMPRINT",EDGE,{"derivedFrom":sQuery(id+"F29.wireOp",EDGE,"E40")}),1.0]])]});
            var Q3;
            Q3=makeQuery(id+"F29.imprint","IMPRINT",FACE,{"disambiguationData":[TD([[makeQuery(id+"F29.imprint","IMPRINT",EDGE,{"derivedFrom":sQuery(id+"F29.wireOp",EDGE,"E41")}),1.0]])]});
            extrude(context, id + "F30", {"entities" : qUnion([Q0, Q1, Q2, Q3]), "depth" : 25 * mm});
        }
        {
            var Q0;
            Q0=makeQuery(id+"F30.opExtrude","CAP_FACE",FACE,{"disambiguationData":[OSD([sQuery(id+"F29.wireOp",EDGE,"E38")])],"isStart":false});
            var sketch = newSketch(context, id + "F31", { "sketchPlane" : qUnion([Q0])});
            skLineSegment(sketch, "E42.bottom", {"start": v(-452.9, 270.4) * mm, "end": v(-577.9, 270.4) * mm});
            skLineSegment(sketch, "E42.top", {"start": v(-452.9, 220.4) * mm, "end": v(-577.9, 220.4) * mm});
            skLineSegment(sketch, "E42.left", {"start": v(-452.9, 270.4) * mm, "end": v(-452.9, 220.4) * mm});
            skLineSegment(sketch, "E42.right", {"start": v(-577.9, 270.4) * mm, "end": v(-577.9, 220.4) * mm});
            skPoint(sketch, "E42.middle", {"position": v(-515.4, 245.4) * mm});
            skSolve(sketch);
        }
        {
            var Q0;
            {var subQ0=sQuery(id+"F31.wireOp",EDGE,"E42.left");Q0=makeQuery(id+"F31.imprint","IMPRINT",FACE,{"disambiguationData":[TD([[makeQuery(id+"F31.imprint","IMPRINT",EDGE,{"derivedFrom":subQ0}),-1.0]])]});}
            var Q1;
            {var subQ0=sQuery(id+"F31.wireOp",EDGE,"E42.bottom");var subQ1=makeQuery(id+"F30.opExtrude","CAP_EDGE",EDGE,{"disambiguationData":[OSD([sQuery(id+"F29.wireOp",EDGE,"E38")])],"isStart":false});var subQ2=makeQuery(id+"F31.imprint","INTERSECT",VERTEX,{"disambiguationData":[OD(0.0)],"derivedFrom":[subQ1,subQ0]});Q1=makeQuery(id+"F31.imprint","IMPRINT",FACE,{"disambiguationData":[TD([[makeQuery(id+"F31.imprint","IMPRINT",EDGE,{"disambiguationData":[TD([[subQ2,-1.0]])],"derivedFrom":subQ0}),1.0]])]});}
            var Q2;
            {var subQ0=sQuery(id+"F31.wireOp",EDGE,"E42.right");Q2=makeQuery(id+"F31.imprint","IMPRINT",FACE,{"disambiguationData":[TD([[makeQuery(id+"F31.imprint","IMPRINT",EDGE,{"derivedFrom":subQ0}),1.0]])]});}
            extrude(context, id + "F32", {"entities" : qUnion([Q0, Q1, Q2]), "depth" : 3 * mm});
        }
        {
            var Q0;
            Q0=makeQuery(id+"F32.opExtrude","CAP_FACE",FACE,{"disambiguationData":[OSD([sQuery(id+"F31.wireOp",EDGE,"E42.bottom"),sQuery(id+"F31.wireOp",EDGE,"E42.top"),sQuery(id+"F31.wireOp",EDGE,"E42.left"),sQuery(id+"F31.wireOp",EDGE,"E42.right")])],"isStart":false});
            var sketch = newSketch(context, id + "F33", { "sketchPlane" : qUnion([Q0])});
            skLineSegment(sketch, "E43.bottom", {"start": v(-577.9, 270.4) * mm, "end": v(-452.9, 270.4) * mm});
            skLineSegment(sketch, "E43.top", {"start": v(-577.9, 267.4) * mm, "end": v(-452.9, 267.4) * mm});
            skLineSegment(sketch, "E43.left", {"start": v(-577.9, 270.4) * mm, "end": v(-577.9, 267.4) * mm});
            skLineSegment(sketch, "E43.right", {"start": v(-452.9, 270.4) * mm, "end": v(-452.9, 267.4) * mm});
            skLineSegment(sketch, "E44.bottom", {"start": v(-577.9, 220.4) * mm, "end": v(-452.9, 220.4) * mm});
            skLineSegment(sketch, "E44.top", {"start": v(-577.9, 223.4) * mm, "end": v(-452.9, 223.4) * mm});
            skLineSegment(sketch, "E44.left", {"start": v(-577.9, 220.4) * mm, "end": v(-577.9, 223.4) * mm});
            skLineSegment(sketch, "E44.right", {"start": v(-452.9, 220.4) * mm, "end": v(-452.9, 223.4) * mm});
            skSolve(sketch);
        }
        {
            var Q0;
            Q0=makeQuery(id+"F33.imprint","IMPRINT",FACE,{"disambiguationData":[TD([[makeQuery(id+"F33.imprint","IMPRINT",EDGE,{"derivedFrom":sQuery(id+"F33.wireOp",EDGE,"E43.bottom")}),1.0]])]});
            var Q1;
            Q1=makeQuery(id+"F33.imprint","IMPRINT",FACE,{"disambiguationData":[TD([[makeQuery(id+"F33.imprint","IMPRINT",EDGE,{"derivedFrom":sQuery(id+"F33.wireOp",EDGE,"E44.bottom")}),-1.0]])]});
            extrude(context, id + "F34", {"entities" : qUnion([Q0, Q1]), "operationType" : NewBodyOperationType.ADD, "depth" : 115 * mm});
        }
        {
            var Q0;
            Q0=makeQuery(id+"F34.boolean.opBoolean","MERGE",FACE,{"derivedFrom":[makeQuery(id+"F32.opExtrude","SWEPT_FACE",FACE,{"disambiguationData":[OSD([sQuery(id+"F31.wireOp",EDGE,"E42.top")])]}),makeQuery(id+"F34.opExtrude","SWEPT_FACE",FACE,{"disambiguationData":[OSD([sQuery(id+"F33.wireOp",EDGE,"E44.bottom")])]})]});
            var sketch = newSketch(context, id + "F35", { "sketchPlane" : qUnion([Q0])});
            skLineSegment(sketch, "E45", {"start": v(527.9, -418) * mm, "end": v(577.9, -300) * mm});
            skLineSegment(sketch, "E46", {"start": v(527.9, -418) * mm, "end": v(502.9, -418) * mm});
            skLineSegment(sketch, "E47", {"start": v(502.9, -418) * mm, "end": v(452.9, -300) * mm});
            skLineSegment(sketch, "E48", {"start": v(502.9, -418) * mm, "end": v(452.9, -418) * mm});
            skLineSegment(sketch, "E49", {"start": v(577.9, -418) * mm, "end": v(527.9, -418) * mm});
            skSolve(sketch);
        }
        {
            var Q0;
            Q0=makeQuery(id+"F35.imprint","IMPRINT",FACE,{"disambiguationData":[TD([[makeQuery(id+"F35.imprint","IMPRINT",EDGE,{"derivedFrom":sQuery(id+"F35.wireOp",EDGE,"E45")}),-1.0]])]});
            var Q1;
            Q1=makeQuery(id+"F35.imprint","IMPRINT",FACE,{"disambiguationData":[TD([[makeQuery(id+"F35.imprint","IMPRINT",EDGE,{"derivedFrom":sQuery(id+"F35.wireOp",EDGE,"E47")}),1.0]])]});
            extrude(context, id + "F36", {"entities" : qUnion([Q0, Q1]), "operationType" : NewBodyOperationType.REMOVE, "oppositeDirection" : true, "depth" : 50 * mm});
        }
        {
            var Q0;
            Q0=makeQuery(id+"F34.opExtrude","SWEPT_FACE",FACE,{"disambiguationData":[OSD([sQuery(id+"F33.wireOp",EDGE,"E43.top")])]});
            var sketch = newSketch(context, id + "F37", { "sketchPlane" : qUnion([Q0])});
            skPoint(sketch, "E50", {"position": v(515.4, -408) * mm});
            skCircle(sketch, "E51", {"center": v(515.4, -408) * mm, "radius": 75 * mm});
            skSolve(sketch);
        }
        {
            var Q0;
            {var subQ1=sQuery(id+"F33.wireOp",EDGE,"E43.top");var subQ7=makeQuery(id+"F34.opExtrude","CAP_EDGE",EDGE,{"disambiguationData":[OSD([subQ1])],"isStart":false});Q0=makeQuery(id+"F37.imprint","IMPRINT",FACE,{"disambiguationData":[TD([[makeQuery(id+"F37.imprint","IMPRINT",EDGE,{"derivedFrom":subQ7}),1.0]])]});}
            var Q1;
            {var subQ1=sQuery(id+"F33.wireOp",EDGE,"E43.top");var subQ7=makeQuery(id+"F34.opExtrude","CAP_EDGE",EDGE,{"disambiguationData":[OSD([subQ1])],"isStart":false});Q1=makeQuery(id+"F37.imprint","IMPRINT",FACE,{"disambiguationData":[TD([[makeQuery(id+"F37.imprint","IMPRINT",EDGE,{"derivedFrom":subQ7}),-1.0]])]});}
            extrude(context, id + "F38", {"entities" : qUnion([Q0, Q1]), "depth" : 44 * mm});
        }
        {
            var Q0;
            Q0=makeQuery(id+"F38.opExtrude","SWEPT_BODY",BODY,{"disambiguationData":[OSD([sQuery(id+"F37.wireOp",EDGE,"E51")])]});
            transform(context, id + "F39", {"entities" : qUnion([Q0]), "transformType" : TransformType.TRANSLATION_3D, "dx" : 0 * mm, "dy" : 491 * mm, "dz" : 0 * mm, "makeCopy" : true});
        }
        {
            var Q0;
            Q0=makeQuery(id+"F32.opExtrude","SWEPT_BODY",BODY,{"disambiguationData":[OSD([sQuery(id+"F31.wireOp",EDGE,"E42.bottom"),sQuery(id+"F31.wireOp",EDGE,"E42.top"),sQuery(id+"F31.wireOp",EDGE,"E42.left"),sQuery(id+"F31.wireOp",EDGE,"E42.right")])]});
            transform(context, id + "F40", {"entities" : qUnion([Q0]), "transformType" : TransformType.TRANSLATION_3D, "dx" : 0 * mm, "dy" : 491 * mm, "dz" : 0 * mm, "makeCopy" : true});
        }
        {
            var Q0;
            Q0=makeQuery(id+"F39.opPattern","COPY",BODY,{"derivedFrom":makeQuery(id+"F38.opExtrude","SWEPT_BODY",BODY,{"disambiguationData":[OSD([sQuery(id+"F37.wireOp",EDGE,"E51")])]}),"instanceName":"1"});
            transform(context, id + "F41", {"entities" : qUnion([Q0]), "transformType" : TransformType.TRANSLATION_3D, "dx" : 1030 * mm, "dy" : 0 * mm, "dz" : 0 * mm, "makeCopy" : true});
        }
        {
            var Q0;
            Q0=makeQuery(id+"F40.opPattern","COPY",BODY,{"derivedFrom":makeQuery(id+"F32.opExtrude","SWEPT_BODY",BODY,{"disambiguationData":[OSD([sQuery(id+"F31.wireOp",EDGE,"E42.bottom"),sQuery(id+"F31.wireOp",EDGE,"E42.top"),sQuery(id+"F31.wireOp",EDGE,"E42.left"),sQuery(id+"F31.wireOp",EDGE,"E42.right")])]}),"instanceName":"1"});
            transform(context, id + "F42", {"entities" : qUnion([Q0]), "transformType" : TransformType.TRANSLATION_3D, "dx" : 1030 * mm, "dy" : 0 * mm, "dz" : 0 * mm, "makeCopy" : true});
        }
        {
            var Q0;
            Q0=makeQuery(id+"F32.opExtrude","SWEPT_BODY",BODY,{"disambiguationData":[OSD([sQuery(id+"F31.wireOp",EDGE,"E42.bottom"),sQuery(id+"F31.wireOp",EDGE,"E42.top"),sQuery(id+"F31.wireOp",EDGE,"E42.left"),sQuery(id+"F31.wireOp",EDGE,"E42.right")])]});
            transform(context, id + "F43", {"entities" : qUnion([Q0]), "transformType" : TransformType.TRANSLATION_3D, "dx" : 1030 * mm, "dy" : 0 * mm, "dz" : 0 * mm, "makeCopy" : true});
        }
        {
            var Q0;
            Q0=makeQuery(id+"F38.opExtrude","SWEPT_BODY",BODY,{"disambiguationData":[OSD([sQuery(id+"F37.wireOp",EDGE,"E51")])]});
            transform(context, id + "F44", {"entities" : qUnion([Q0]), "transformType" : TransformType.TRANSLATION_3D, "dx" : 1030 * mm, "dy" : 0 * mm, "dz" : 0 * mm, "makeCopy" : true});
        }
        {
            var Q0;
            Q0=makeQuery(id+"F4.opShell","OFFSET_FACE",FACE,{"disambiguationData":[OSD([sQuery(id+"F0.wireOp",EDGE,"E1.bottom"),sQuery(id+"F0.wireOp",EDGE,"E1.top"),sQuery(id+"F0.wireOp",EDGE,"E1.left"),sQuery(id+"F0.wireOp",EDGE,"E1.right")])]});
            extrude(context, id + "F45", {"entities" : qUnion([Q0]), "depth" : 2 * mm, "offsetDistance" : 25 * mm});
        }
        {
            var Q0;
            Q0=makeQuery(id+"F45.opExtrude","SWEPT_BODY",BODY,{"disambiguationData":[OSD([sQuery(id+"F0.wireOp",EDGE,"E1.bottom"),sQuery(id+"F0.wireOp",EDGE,"E1.top"),sQuery(id+"F0.wireOp",EDGE,"E1.left"),sQuery(id+"F0.wireOp",EDGE,"E1.right")])]});
            transform(context, id + "F46", {"entities" : qUnion([Q0]), "transformType" : TransformType.TRANSLATION_3D, "dx" : 0 * mm, "dy" : 0 * mm, "dz" : 599 * mm, "makeCopy" : false});
        }
        {
            var Q0;
            Q0=makeQuery(id+"F20.opExtrude","CAP_FACE",FACE,{"disambiguationData":[OSD([sQuery(id+"F19.wireOp",EDGE,"E24.bottom"),sQuery(id+"F19.wireOp",EDGE,"E24.top"),sQuery(id+"F19.wireOp",EDGE,"E24.left"),sQuery(id+"F19.wireOp",EDGE,"E24.right")])],"isStart":false});
            var Q1;
            Q1=makeQuery(id+"F20.opExtrude","CAP_FACE",FACE,{"disambiguationData":[OSD([sQuery(id+"F19.wireOp",EDGE,"E23.bottom"),sQuery(id+"F19.wireOp",EDGE,"E23.top"),sQuery(id+"F19.wireOp",EDGE,"E23.left"),sQuery(id+"F19.wireOp",EDGE,"E23.right")])],"isStart":false});
            extrude(context, id + "F47", {"entities" : qUnion([Q0, Q1]), "operationType" : NewBodyOperationType.ADD, "depth" : 130 * mm, "offsetDistance" : 25 * mm});
        }
        {
            var Q0;
            Q0=makeQuery(id+"F45.opExtrude","CAP_FACE",FACE,{"disambiguationData":[OSD([sQuery(id+"F0.wireOp",EDGE,"E1.bottom"),sQuery(id+"F0.wireOp",EDGE,"E1.top"),sQuery(id+"F0.wireOp",EDGE,"E1.left"),sQuery(id+"F0.wireOp",EDGE,"E1.right")])],"isStart":false});
            var sketch = newSketch(context, id + "F48", { "sketchPlane" : qUnion([Q0])});
            skLineSegment(sketch, "E52", {"start": v(-557, 287) * mm, "end": v(557, -287) * mm, "construction": true});
            skLineSegment(sketch, "E53", {"start": v(-557, -287) * mm, "end": v(557, 287) * mm, "construction": true});
            skLineSegment(sketch, "E54.bottom", {"start": v(-150, 50) * mm, "end": v(150, 50) * mm});
            skLineSegment(sketch, "E54.top", {"start": v(-150, -50) * mm, "end": v(150, -50) * mm});
            skLineSegment(sketch, "E54.left", {"start": v(-150, 50) * mm, "end": v(-150, -50) * mm});
            skLineSegment(sketch, "E54.right", {"start": v(150, 50) * mm, "end": v(150, -50) * mm});
            skPoint(sketch, "E54.middle", {"position": v(0, 0) * mm});
            skSolve(sketch);
        }
        {
            var Q0;
            Q0=makeQuery(id+"F48.imprint","IMPRINT",FACE,{"disambiguationData":[TD([[makeQuery(id+"F48.imprint","IMPRINT",EDGE,{"derivedFrom":sQuery(id+"F48.wireOp",EDGE,"E54.bottom")}),-1.0]])]});
            extrude(context, id + "F49", {"entities" : qUnion([Q0]), "operationType" : NewBodyOperationType.REMOVE, "oppositeDirection" : true, "depth" : 3 * mm, "offsetDistance" : 25 * mm});
        }
    });
